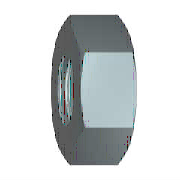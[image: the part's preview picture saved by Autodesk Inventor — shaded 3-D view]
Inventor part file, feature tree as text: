
AUTODESK INVENTOR PART (.ipt)
format: ipt  version: 2015 (Build 190159000, 159)  size: 160,768 bytes
history: native  units: mm (DEFAULTED — no unit token found)
features: sketch x3, chamfer x1, hole x1, other x1, plane x1
ambient origin geometry x7: Origin, YZ Plane, XZ Plane, X Axis, Y Axis, Z Axis, Center Point
bodies: Solid1 (feature_tree), Body (feature_tree)
feature tree (7):
  chamfer  "Chamfer1"  Angle=30.0deg  [1 undecoded]
  hole  "Thread"  [1 undecoded]
  other  "Work Axis1"
  plane  "Work Plane1"
  sketch  "Sketch1"  dims[d0=15.011107mm]
  sketch  "Sketch2"  dims[d1=6.5mm]
  sketch  "Sketch3"  dims[d2=0.0mm d3=30.0deg d4=30.0deg d5=11.3mm d6=11.3mm d7=90.0deg d25=6.647mm d26=6.0mm d27=4.0mm d28=2.0mm d29=14.3117mm d30=8.0mm d31=20.594885mm d8=0.676582mm d9=30.0deg d10=0.676582mm d11=30.0deg d13=0.0mm d14=0.0mm d39=0.0mm d40=0.676582mm d41=0.676582mm d42=0.0mm]
note: 2 required parameter values undecoded (feature->parameter linkage not recoverable at this tier; creation-order binding heuristic only, values carry confidence <= 0.55)
